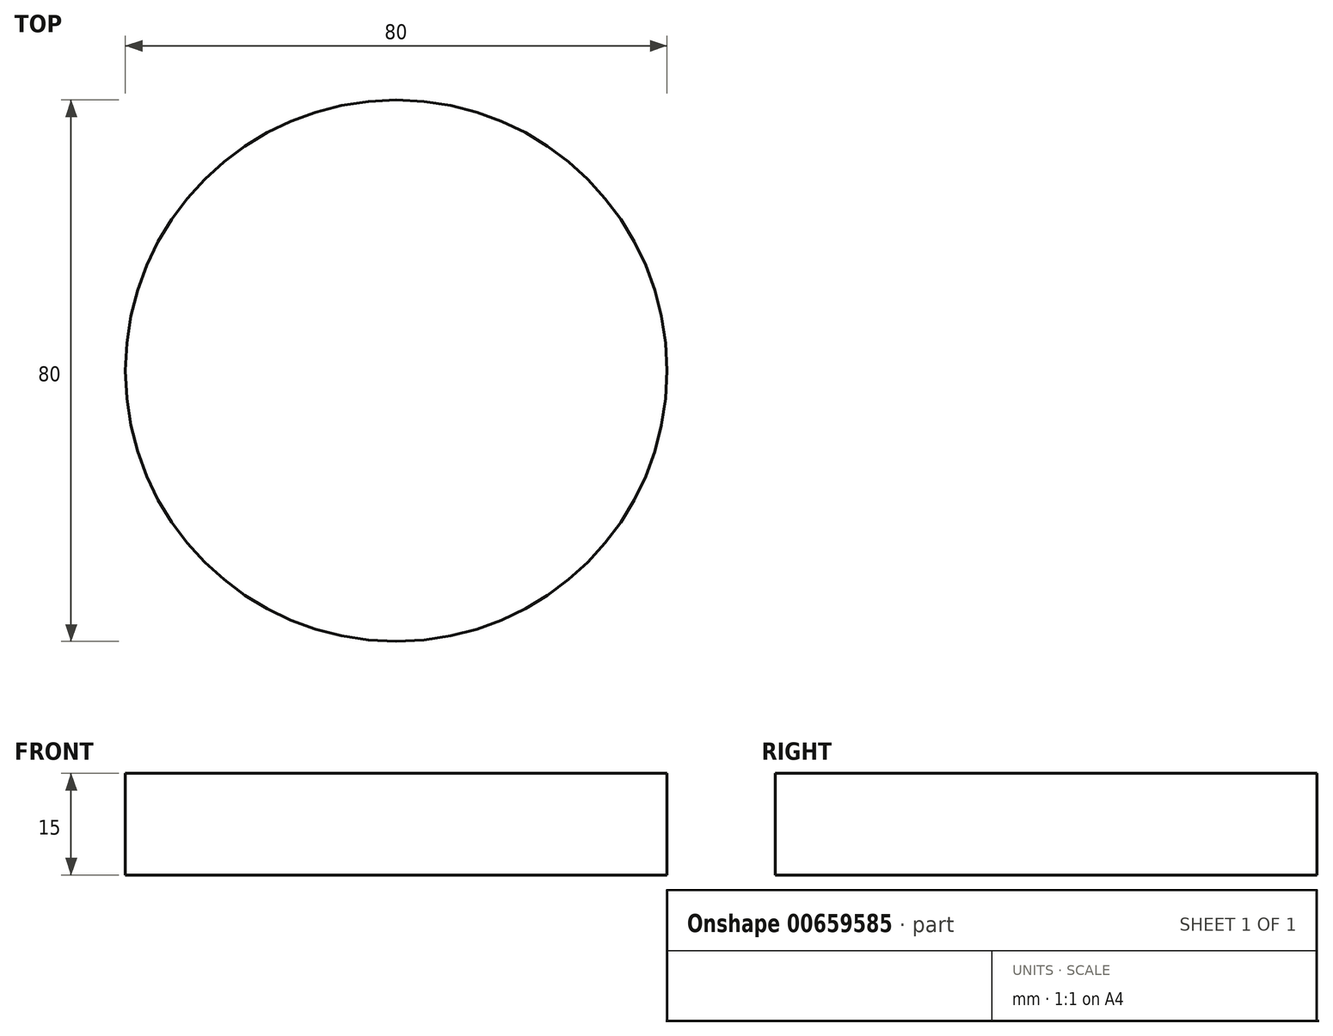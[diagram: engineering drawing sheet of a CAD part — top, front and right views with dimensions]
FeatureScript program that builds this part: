
annotation { "Feature Type Name" : "Feature", "Feature Type Description" : "" }
export const myFeature = defineFeature(function(context is Context, id is Id, definition is map)
    precondition{}
    {
        {
            var Q0;
            Q0=qCreatedBy(makeId("Top.planeOp"),FACE);
            var sketch = newSketch(context, id + "F0", { "sketchPlane" : qUnion([Q0])});
            skCircle(sketch, "E0", {"center": v(0, 0) * mm, "radius": 40 * mm});
            skSolve(sketch);
        }
        {
            var Q0;
            Q0 = qSketchRegion(id + "F0", true);
            extrude(context, id + "F1", {"entities" : qUnion([Q0]), "depth" : 15 * mm, "offsetDistance" : 25 * mm});
        }
    });
